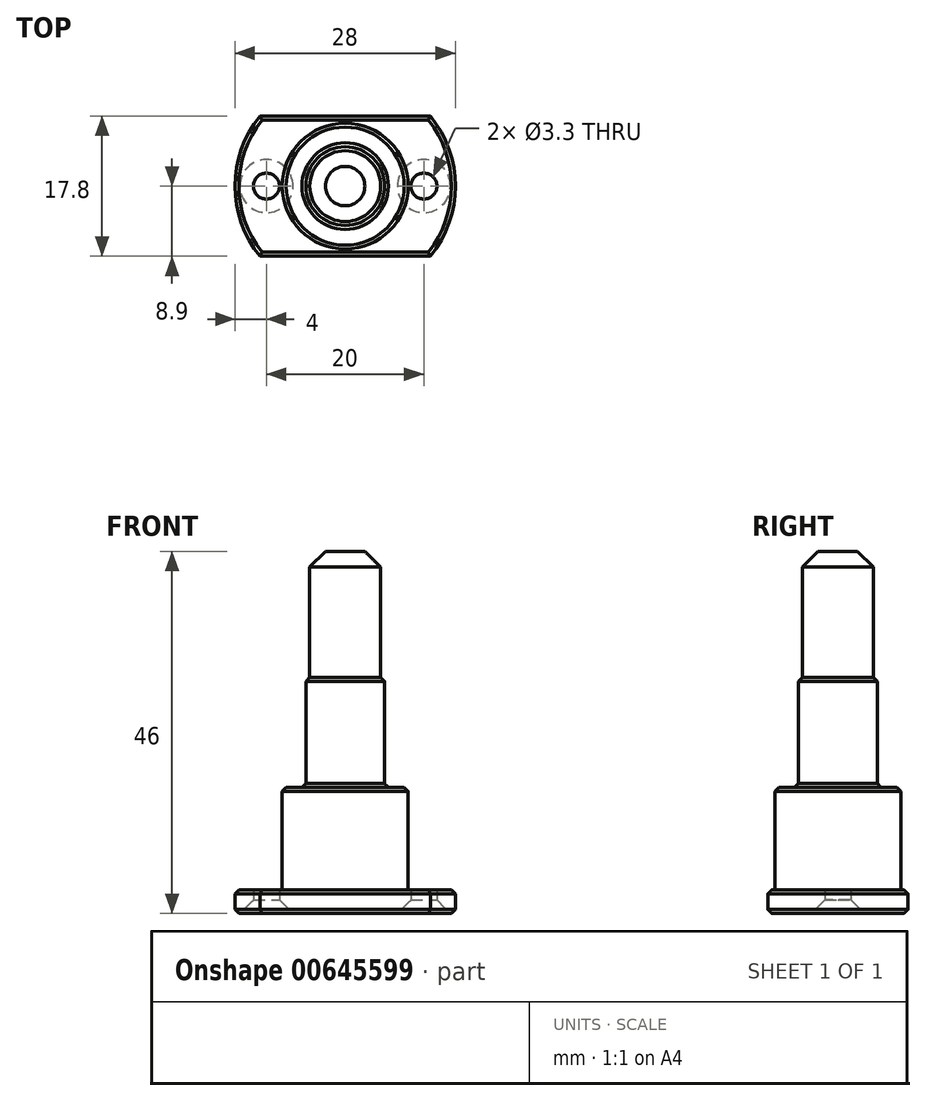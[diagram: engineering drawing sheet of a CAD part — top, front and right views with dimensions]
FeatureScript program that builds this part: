
annotation { "Feature Type Name" : "Feature", "Feature Type Description" : "" }
export const myFeature = defineFeature(function(context is Context, id is Id, definition is map)
    precondition{}
    {
        {
            var Q0;
            Q0=qCreatedBy(makeId("Top.planeOp"),FACE);
            var sketch = newSketch(context, id + "F0", { "sketchPlane" : qUnion([Q0])});
            skArc(sketch, "E0", {"start": v(-10.8, 8.9) * mm, "mid": v(-14, 0) * mm, "end": v(-10.8, -8.9) * mm});
            skLineSegment(sketch, "E1", {"start": v(-10.8, 8.9) * mm, "end": v(10.8, 8.9) * mm});
            skLineSegment(sketch, "E2.MirrorCS", {"start": v(-10.8, -8.9) * mm, "end": v(10.8, -8.9) * mm});
            skArc(sketch, "E3.trimOffspring", {"start": v(10.8, -8.9) * mm, "mid": v(14, 0) * mm, "end": v(10.8, 8.9) * mm});
            skSolve(sketch);
        }
        {
            var Q0;
            Q0 = qSketchRegion(id + "F0", true);
            extrude(context, id + "F1", {"entities" : qUnion([Q0]), "depth" : 3 * mm, "offsetDistance" : 25.4 * mm});
        }
        {
            var Q0;
            Q0=qCreatedBy(makeId("Top.planeOp"),FACE);
            var sketch = newSketch(context, id + "F2", { "sketchPlane" : qUnion([Q0])});
            skPoint(sketch, "E4", {"position": v(-10, 0) * mm});
            skPoint(sketch, "E5.MirrorP", {"position": v(10, 0) * mm});
            skSolve(sketch);
        }
        {
            var Q0;
            Q0=sQuery(id+"F2.wireOp",VERTEX,"E4");
            var Q1;
            Q1=sQuery(id+"F2.wireOp",VERTEX,"E5.MirrorP");
            var Q2;
            Q2=makeQuery(id+"F1.opExtrude","SWEPT_BODY",BODY,{"disambiguationData":[OSD([sQuery(id+"F0.wireOp",EDGE,"E0"),sQuery(id+"F0.wireOp",EDGE,"E1"),sQuery(id+"F0.wireOp",EDGE,"E2.MirrorCS"),sQuery(id+"F0.wireOp",EDGE,"E3.trimOffspring")])]});
            hole(context, id + "F3", {"style" : HoleStyle.C_SINK, "endStyle" : HoleEndStyle.THROUGH, "oppositeDirection" : true, "standardTappedOrClearance" : lookupTablePath({ "standard" : "ISO", "fit" : "Normal", "size" : "M3", "type" : "Clearance" }), "standardBlindInLast" : lookupTablePath({ "fit" : "Standard", "standard" : "ISO", "size" : "M3", "type" : "Clearance" }), "holeDiameter" : 3.3 * mm, "cSinkDiameter" : 6.72 * mm, "cSinkAngle" : 90 * degree, "majorDiameter" : 6.35 * mm, "isTappedThrough" : true, "tappedDepth" : 12.7 * mm, "tapClearance" : 3, "locations" : qUnion([Q0, Q1]), "scope" : qUnion([Q2])});
        }
        {
            var Q0;
            Q0=makeQuery(id+"F1.opExtrude","CAP_FACE",FACE,{"disambiguationData":[OSD([sQuery(id+"F0.wireOp",EDGE,"E0"),sQuery(id+"F0.wireOp",EDGE,"E1"),sQuery(id+"F0.wireOp",EDGE,"E2.MirrorCS"),sQuery(id+"F0.wireOp",EDGE,"E3.trimOffspring")])],"isStart":false});
            var sketch = newSketch(context, id + "F4", { "sketchPlane" : qUnion([Q0])});
            skCircle(sketch, "E6", {"center": v(0, 0) * mm, "radius": 8 * mm});
            skSolve(sketch);
        }
        {
            var Q0;
            Q0=makeQuery(id+"F4.imprint","IMPRINT",FACE,{"disambiguationData":[TD([[makeQuery(id+"F4.imprint","IMPRINT",EDGE,{"derivedFrom":sQuery(id+"F4.wireOp",EDGE,"E6")}),1.0]])]});
            extrude(context, id + "F5", {"entities" : qUnion([Q0]), "operationType" : NewBodyOperationType.ADD, "depth" : 13 * mm, "offsetDistance" : 25.4 * mm});
        }
        {
            var Q0;
            Q0=makeQuery(id+"F1.opExtrude","CAP_EDGE",EDGE,{"disambiguationData":[OSD([sQuery(id+"F0.wireOp",EDGE,"E1")])],"isStart":false});
            var Q1;
            Q1=makeQuery(id+"F1.opExtrude","CAP_EDGE",EDGE,{"disambiguationData":[OSD([sQuery(id+"F0.wireOp",EDGE,"E3.trimOffspring")])],"isStart":false});
            var Q2;
            Q2=makeQuery(id+"F1.opExtrude","CAP_EDGE",EDGE,{"disambiguationData":[OSD([sQuery(id+"F0.wireOp",EDGE,"E2.MirrorCS")])],"isStart":false});
            var Q3;
            Q3=makeQuery(id+"F1.opExtrude","CAP_EDGE",EDGE,{"disambiguationData":[OSD([sQuery(id+"F0.wireOp",EDGE,"E0")])],"isStart":false});
            chamfer(context, id + "F6", {"entities" : qUnion([Q0, Q1, Q2, Q3]), "chamferType" : ChamferType.OFFSET_ANGLE, "width" : 0.5 * mm, "oppositeDirection" : false, "angle" : 45 * degree, "tangentPropagation" : true});
        }
        {
            var Q0;
            Q0=makeQuery(id+"F5.opExtrude","CAP_FACE",FACE,{"disambiguationData":[OSD([sQuery(id+"F4.wireOp",EDGE,"E6")])],"isStart":false});
            var sketch = newSketch(context, id + "F7", { "sketchPlane" : qUnion([Q0])});
            skCircle(sketch, "E7", {"center": v(0, 0) * mm, "radius": 5 * mm});
            skSolve(sketch);
        }
        {
            var Q0;
            Q0=makeQuery(id+"F7.imprint","IMPRINT",FACE,{"disambiguationData":[TD([[makeQuery(id+"F7.imprint","IMPRINT",EDGE,{"derivedFrom":sQuery(id+"F7.wireOp",EDGE,"E7")}),1.0]])]});
            extrude(context, id + "F8", {"entities" : qUnion([Q0]), "operationType" : NewBodyOperationType.ADD, "depth" : 14 * mm, "offsetDistance" : 25.4 * mm});
        }
        {
            var Q0;
            Q0=makeQuery(id+"F8.opExtrude","CAP_FACE",FACE,{"disambiguationData":[OSD([sQuery(id+"F7.wireOp",EDGE,"E7")])],"isStart":false});
            var sketch = newSketch(context, id + "F9", { "sketchPlane" : qUnion([Q0])});
            skCircle(sketch, "E8", {"center": v(0, 0) * mm, "radius": 4.5 * mm});
            skSolve(sketch);
        }
        {
            var Q0;
            Q0=makeQuery(id+"F9.imprint","IMPRINT",FACE,{"disambiguationData":[TD([[makeQuery(id+"F9.imprint","IMPRINT",EDGE,{"derivedFrom":sQuery(id+"F9.wireOp",EDGE,"E8")}),1.0]])]});
            extrude(context, id + "F10", {"entities" : qUnion([Q0]), "operationType" : NewBodyOperationType.ADD, "depth" : 16 * mm, "offsetDistance" : 25.4 * mm});
        }
        {
            var Q0;
            Q0=makeQuery(id+"F8.opExtrude","CAP_EDGE",EDGE,{"disambiguationData":[OSD([sQuery(id+"F7.wireOp",EDGE,"E7")])],"isStart":false});
            var Q1;
            Q1=makeQuery(id+"F5.opExtrude","CAP_EDGE",EDGE,{"disambiguationData":[OSD([sQuery(id+"F4.wireOp",EDGE,"E6")])],"isStart":false});
            var Q2;
            Q2=makeQuery(id+"F5.opExtrude","CAP_FACE",FACE,{"disambiguationData":[OSD([sQuery(id+"F4.wireOp",EDGE,"E6")])],"isStart":false});
            var Q3;
            Q3=makeQuery(id+"F1.opExtrude","CAP_EDGE",EDGE,{"disambiguationData":[OSD([sQuery(id+"F0.wireOp",EDGE,"E1")])],"isStart":true});
            var Q4;
            Q4=makeQuery(id+"F1.opExtrude","CAP_EDGE",EDGE,{"disambiguationData":[OSD([sQuery(id+"F0.wireOp",EDGE,"E3.trimOffspring")])],"isStart":true});
            var Q5;
            Q5=makeQuery(id+"F1.opExtrude","CAP_EDGE",EDGE,{"disambiguationData":[OSD([sQuery(id+"F0.wireOp",EDGE,"E0")])],"isStart":true});
            var Q6;
            Q6=makeQuery(id+"F1.opExtrude","CAP_EDGE",EDGE,{"disambiguationData":[OSD([sQuery(id+"F0.wireOp",EDGE,"E2.MirrorCS")])],"isStart":true});
            chamfer(context, id + "F11", {"entities" : qUnion([Q0, Q1, Q2, Q3, Q4, Q5, Q6]), "chamferType" : ChamferType.OFFSET_ANGLE, "width" : 0.5 * mm, "oppositeDirection" : false, "angle" : 45 * degree, "tangentPropagation" : true});
        }
        {
            var Q0;
            Q0=makeQuery(id+"F10.opExtrude","CAP_FACE",FACE,{"disambiguationData":[OSD([sQuery(id+"F9.wireOp",EDGE,"E8")])],"isStart":false});
            chamfer(context, id + "F12", {"entities" : qUnion([Q0]), "chamferType" : ChamferType.OFFSET_ANGLE, "width" : 2 * mm, "oppositeDirection" : false, "angle" : 45 * degree, "tangentPropagation" : true});
        }
    });
